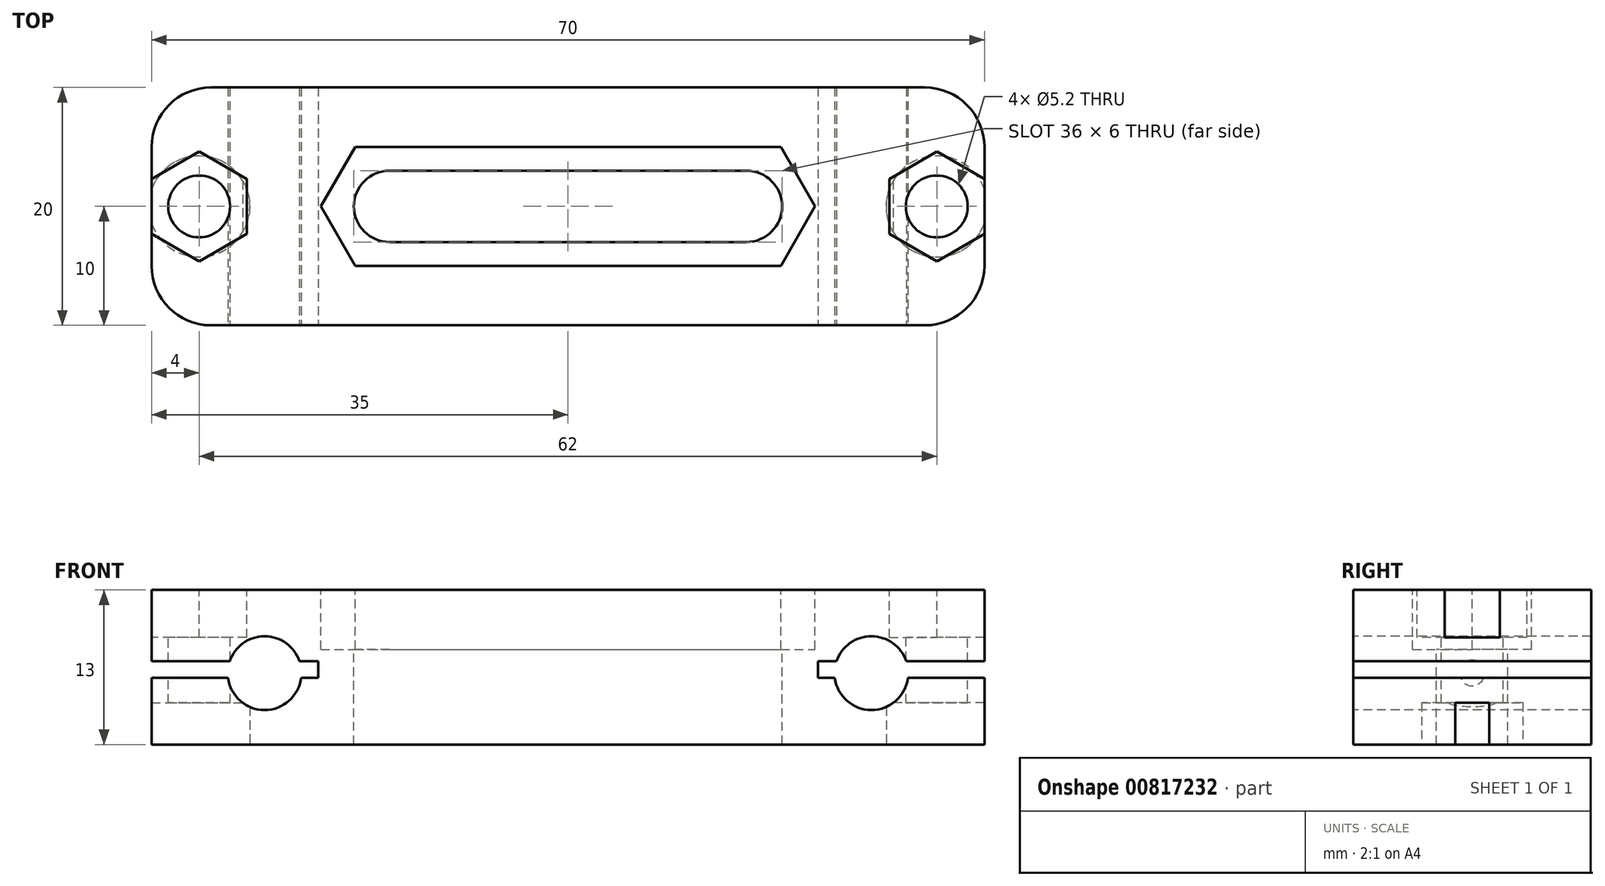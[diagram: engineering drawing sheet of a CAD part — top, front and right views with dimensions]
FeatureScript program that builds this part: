
annotation { "Feature Type Name" : "Feature", "Feature Type Description" : "" }
export const myFeature = defineFeature(function(context is Context, id is Id, definition is map)
    precondition{}
    {
        {
            var Q0;
            Q0=qCreatedBy(makeId("Top.planeOp"),FACE);
            var sketch = newSketch(context, id + "F0", { "sketchPlane" : qUnion([Q0])});
            skLineSegment(sketch, "E0.bottom", {"start": v(35, -10) * mm, "end": v(-35, -10) * mm});
            skLineSegment(sketch, "E0.top", {"start": v(35, 10) * mm, "end": v(-35, 10) * mm});
            skLineSegment(sketch, "E0.left", {"start": v(35, -10) * mm, "end": v(35, 10) * mm});
            skLineSegment(sketch, "E0.right", {"start": v(-35, -10) * mm, "end": v(-35, 10) * mm});
            skPoint(sketch, "E0.middle", {"position": v(0, 0) * mm});
            skSolve(sketch);
        }
        {
            var Q0;
            Q0=qSketchRegion(id+"F0",true);
            extrude(context, id + "F1", {"entities" : qUnion([Q0]), "endBound" : BoundingType.SYMMETRIC, "depth" : 13 * mm, "offsetDistance" : 25 * mm});
        }
        {
            var Q0;
            Q0=makeQuery(id+"F1.opExtrude","CAP_FACE",FACE,{"disambiguationData":[OSD([sQuery(id+"F0.wireOp",EDGE,"E0.bottom"),sQuery(id+"F0.wireOp",EDGE,"E0.top"),sQuery(id+"F0.wireOp",EDGE,"E0.left"),sQuery(id+"F0.wireOp",EDGE,"E0.right")])],"isStart":false});
            var sketch = newSketch(context, id + "F2", { "sketchPlane" : qUnion([Q0])});
            skLineSegment(sketch, "E1.bottom", {"start": v(15, -3) * mm, "end": v(-15, -3) * mm});
            skLineSegment(sketch, "E1.top", {"start": v(15, 3) * mm, "end": v(-15, 3) * mm});
            skPoint(sketch, "E1.middle", {"position": v(0, 0) * mm});
            skArc(sketch, "E2", {"start": v(-15, 3) * mm, "mid": v(-18, 0) * mm, "end": v(-15, -3) * mm});
            skArc(sketch, "E3", {"start": v(15, 3) * mm, "mid": v(18, 0) * mm, "end": v(15, -3) * mm});
            skSolve(sketch);
        }
        {
            var Q0;
            Q0=makeQuery(id+"F2.imprint","IMPRINT",FACE,{"disambiguationData":[TD([[makeQuery(id+"F2.imprint","IMPRINT",EDGE,{"derivedFrom":sQuery(id+"F2.wireOp",EDGE,"E1.bottom")}),1.0]])]});
            var sketch = newSketch(context, id + "F3", { "sketchPlane" : qUnion([Q0])});
            skCircle(sketch, "E4.cCircle", {"center": v(-31, 0) * mm, "radius": 4 * mm, "construction": true});
            skLineSegment(sketch, "E4.0", {"start": v(-27, -2.3) * mm, "end": v(-31, -4.62) * mm});
            skLineSegment(sketch, "E4.1", {"start": v(-31, -4.62) * mm, "end": v(-35, -2.3) * mm});
            skLineSegment(sketch, "E4.2", {"start": v(-35, -2.3) * mm, "end": v(-35, 2.3) * mm});
            skLineSegment(sketch, "E4.3", {"start": v(-35, 2.3) * mm, "end": v(-31, 4.62) * mm});
            skLineSegment(sketch, "E4.4", {"start": v(-31, 4.62) * mm, "end": v(-27, 2.3) * mm});
            skLineSegment(sketch, "E4.5", {"start": v(-27, 2.3) * mm, "end": v(-27, -2.3) * mm});
            skPoint(sketch, "E4.0.midPoint", {"position": v(-29, -3.46) * mm});
            skCircle(sketch, "E5.cCircle", {"center": v(31, 0) * mm, "radius": 4 * mm, "construction": true});
            skLineSegment(sketch, "E5.0", {"start": v(35, 2.3) * mm, "end": v(35, -2.3) * mm});
            skLineSegment(sketch, "E5.1", {"start": v(35, -2.3) * mm, "end": v(31, -4.62) * mm});
            skLineSegment(sketch, "E5.2", {"start": v(31, -4.62) * mm, "end": v(27, -2.3) * mm});
            skLineSegment(sketch, "E5.3", {"start": v(27, -2.3) * mm, "end": v(27, 2.3) * mm});
            skLineSegment(sketch, "E5.4", {"start": v(27, 2.3) * mm, "end": v(31, 4.62) * mm});
            skLineSegment(sketch, "E5.5", {"start": v(31, 4.62) * mm, "end": v(35, 2.3) * mm});
            skPoint(sketch, "E5.0.midPoint", {"position": v(35, 0) * mm});
            skSolve(sketch);
        }
        {
            var Q0;
            Q0=qSketchRegion(id+"F3",true);
            extrude(context, id + "F4", {"entities" : qUnion([Q0]), "operationType" : NewBodyOperationType.REMOVE, "oppositeDirection" : true, "depth" : 4 * mm, "offsetDistance" : 25 * mm});
        }
        {
            var Q0;
            Q0=makeQuery(id+"F2.imprint","IMPRINT",FACE,{"disambiguationData":[TD([[makeQuery(id+"F2.imprint","IMPRINT",EDGE,{"derivedFrom":sQuery(id+"F2.wireOp",EDGE,"E1.bottom")}),1.0]])]});
            var sketch = newSketch(context, id + "F5", { "sketchPlane" : qUnion([Q0])});
            skCircle(sketch, "E6", {"center": v(-31, 0) * mm, "radius": 2.6 * mm});
            skCircle(sketch, "E7", {"center": v(31, 0) * mm, "radius": 2.6 * mm});
            skSolve(sketch);
        }
        {
            var Q0;
            Q0=qSketchRegion(id+"F5",true);
            extrude(context, id + "F6", {"entities" : qUnion([Q0]), "operationType" : NewBodyOperationType.REMOVE, "endBound" : BoundingType.THROUGH_ALL, "oppositeDirection" : true, "depth" : 25 * mm, "offsetDistance" : 25 * mm});
        }
        {
            var Q0;
            Q0=qSketchRegion(id+"F2",true);
            extrude(context, id + "F7", {"entities" : qUnion([Q0]), "operationType" : NewBodyOperationType.REMOVE, "endBound" : BoundingType.THROUGH_ALL, "oppositeDirection" : true, "depth" : 25 * mm, "offsetDistance" : 25 * mm});
        }
        {
            var Q0;
            Q0=makeQuery(id+"F1.opExtrude","SWEPT_FACE",FACE,{"disambiguationData":[OSD([sQuery(id+"F0.wireOp",EDGE,"E0.bottom")])]});
            var sketch = newSketch(context, id + "F8", { "sketchPlane" : qUnion([Q0])});
            skLineSegment(sketch, "E8.bottom", {"start": v(-35, -0.9) * mm, "end": v(-21, -0.9) * mm});
            skLineSegment(sketch, "E8.top", {"start": v(-35, 0.5) * mm, "end": v(-21, 0.5) * mm});
            skLineSegment(sketch, "E8.left", {"start": v(-35, -0.9) * mm, "end": v(-35, 0.5) * mm});
            skLineSegment(sketch, "E8.right", {"start": v(-21, -0.9) * mm, "end": v(-21, 0.5) * mm});
            skLineSegment(sketch, "E9.bottom", {"start": v(35, -0.9) * mm, "end": v(21, -0.9) * mm});
            skLineSegment(sketch, "E9.top", {"start": v(35, 0.5) * mm, "end": v(21, 0.5) * mm});
            skLineSegment(sketch, "E9.left", {"start": v(35, -0.9) * mm, "end": v(35, 0.5) * mm});
            skLineSegment(sketch, "E9.right", {"start": v(21, -0.9) * mm, "end": v(21, 0.5) * mm});
            skSolve(sketch);
        }
        {
            var Q0;
            Q0=qSketchRegion(id+"F8",true);
            extrude(context, id + "F9", {"entities" : qUnion([Q0]), "operationType" : NewBodyOperationType.REMOVE, "endBound" : BoundingType.THROUGH_ALL, "oppositeDirection" : true, "depth" : 25 * mm, "offsetDistance" : 25 * mm});
        }
        {
            var Q0;
            Q0=makeQuery(id+"F1.opExtrude","SWEPT_FACE",FACE,{"disambiguationData":[OSD([sQuery(id+"F0.wireOp",EDGE,"E0.bottom")])]});
            var sketch = newSketch(context, id + "F10", { "sketchPlane" : qUnion([Q0])});
            skCircle(sketch, "E10", {"center": v(-25.5, -0.5) * mm, "radius": 3.1 * mm});
            skCircle(sketch, "E11", {"center": v(25.5, -0.5) * mm, "radius": 3.1 * mm});
            skSolve(sketch);
        }
        {
            var Q0;
            Q0=makeQuery(id+"FGKyORt9fG3GxLQ_1.opExtrude","CAP_EDGE",EDGE,{"disambiguationData":[OSD([sQuery(id+"FUYUVBWRlq5jCbc_1.wireOp",EDGE,"ZpnfMVQ8-PDP1-Nz7W-Utch-BhDVuRkNCdpB.left")])],"isStart":false});
            var Q1;
            {var subQ0=sQuery(id+"F0.wireOp",EDGE,"E0.left");var subQ1=sQuery(id+"F0.wireOp",EDGE,"E0.top");Q1=makeQuery(id+"F9.boolean.opBoolean","SPLIT",EDGE,{"disambiguationData":[TD([makeQuery(id+"F9.opExtrude","SWEPT_FACE",FACE,{"disambiguationData":[OSD([sQuery(id+"F8.wireOp",EDGE,"E9.top")])]})])],"derivedFrom":makeQuery(id+"F1.opExtrude","SWEPT_EDGE",EDGE,{"disambiguationData":[OSD([subQ1,subQ0])]})});}
            var Q2;
            {var subQ0=sQuery(id+"F0.wireOp",EDGE,"E0.left");var subQ1=sQuery(id+"F0.wireOp",EDGE,"E0.top");Q2=makeQuery(id+"F9.boolean.opBoolean","SPLIT",EDGE,{"disambiguationData":[TD([makeQuery(id+"F9.opExtrude","SWEPT_FACE",FACE,{"disambiguationData":[OSD([sQuery(id+"F8.wireOp",EDGE,"E9.bottom")])]})])],"derivedFrom":makeQuery(id+"F1.opExtrude","SWEPT_EDGE",EDGE,{"disambiguationData":[OSD([subQ1,subQ0])]})});}
            var Q3;
            {var subQ0=sQuery(id+"F0.wireOp",EDGE,"E0.bottom");var subQ1=sQuery(id+"F0.wireOp",EDGE,"E0.left");Q3=makeQuery(id+"F9.boolean.opBoolean","SPLIT",EDGE,{"disambiguationData":[TD([makeQuery(id+"F9.opExtrude","SWEPT_FACE",FACE,{"disambiguationData":[OSD([sQuery(id+"F8.wireOp",EDGE,"E9.top")])]})])],"derivedFrom":makeQuery(id+"F1.opExtrude","SWEPT_EDGE",EDGE,{"disambiguationData":[OSD([subQ0,subQ1])]})});}
            var Q4;
            {var subQ0=sQuery(id+"F0.wireOp",EDGE,"E0.bottom");var subQ1=sQuery(id+"F0.wireOp",EDGE,"E0.left");Q4=makeQuery(id+"F9.boolean.opBoolean","SPLIT",EDGE,{"disambiguationData":[TD([makeQuery(id+"F9.opExtrude","SWEPT_FACE",FACE,{"disambiguationData":[OSD([sQuery(id+"F8.wireOp",EDGE,"E9.bottom")])]})])],"derivedFrom":makeQuery(id+"F1.opExtrude","SWEPT_EDGE",EDGE,{"disambiguationData":[OSD([subQ0,subQ1])]})});}
            var Q5;
            {var subQ0=sQuery(id+"F0.wireOp",EDGE,"E0.bottom");var subQ1=sQuery(id+"F0.wireOp",EDGE,"E0.right");Q5=makeQuery(id+"F9.boolean.opBoolean","SPLIT",EDGE,{"disambiguationData":[TD([makeQuery(id+"F9.opExtrude","SWEPT_FACE",FACE,{"disambiguationData":[OSD([sQuery(id+"F8.wireOp",EDGE,"E8.bottom")])]})])],"derivedFrom":makeQuery(id+"F1.opExtrude","SWEPT_EDGE",EDGE,{"disambiguationData":[OSD([subQ0,subQ1])]})});}
            var Q6;
            {var subQ0=sQuery(id+"F0.wireOp",EDGE,"E0.bottom");var subQ1=sQuery(id+"F0.wireOp",EDGE,"E0.right");Q6=makeQuery(id+"F9.boolean.opBoolean","SPLIT",EDGE,{"disambiguationData":[TD([makeQuery(id+"F9.opExtrude","SWEPT_FACE",FACE,{"disambiguationData":[OSD([sQuery(id+"F8.wireOp",EDGE,"E8.top")])]})])],"derivedFrom":makeQuery(id+"F1.opExtrude","SWEPT_EDGE",EDGE,{"disambiguationData":[OSD([subQ0,subQ1])]})});}
            var Q7;
            {var subQ0=sQuery(id+"F0.wireOp",EDGE,"E0.right");var subQ1=sQuery(id+"F0.wireOp",EDGE,"E0.top");Q7=makeQuery(id+"F9.boolean.opBoolean","SPLIT",EDGE,{"disambiguationData":[TD([makeQuery(id+"F9.opExtrude","SWEPT_FACE",FACE,{"disambiguationData":[OSD([sQuery(id+"F8.wireOp",EDGE,"E8.top")])]})])],"derivedFrom":makeQuery(id+"F1.opExtrude","SWEPT_EDGE",EDGE,{"disambiguationData":[OSD([subQ1,subQ0])]})});}
            var Q8;
            {var subQ0=sQuery(id+"F0.wireOp",EDGE,"E0.right");var subQ1=sQuery(id+"F0.wireOp",EDGE,"E0.top");Q8=makeQuery(id+"F9.boolean.opBoolean","SPLIT",EDGE,{"disambiguationData":[TD([makeQuery(id+"F9.opExtrude","SWEPT_FACE",FACE,{"disambiguationData":[OSD([sQuery(id+"F8.wireOp",EDGE,"E8.bottom")])]})])],"derivedFrom":makeQuery(id+"F1.opExtrude","SWEPT_EDGE",EDGE,{"disambiguationData":[OSD([subQ1,subQ0])]})});}
            var Q9;
            Q9=makeQuery(id+"FGKyORt9fG3GxLQ_1.opExtrude","CAP_EDGE",EDGE,{"disambiguationData":[OSD([sQuery(id+"FUYUVBWRlq5jCbc_1.wireOp",EDGE,"ZpnfMVQ8-PDP1-Nz7W-Utch-BhDVuRkNCdpB.right")])],"isStart":false});
            fillet(context, id + "F11", {"entities" : qUnion([Q0, Q1, Q2, Q3, Q4, Q5, Q6, Q7, Q8, Q9]), "radius" : 5 * mm, "tangentPropagation" : true, "allowEdgeOverflow" : false});
        }
        {
            var Q0;
            Q0=qSketchRegion(id+"F10",true);
            extrude(context, id + "F12", {"entities" : qUnion([Q0]), "operationType" : NewBodyOperationType.REMOVE, "endBound" : BoundingType.THROUGH_ALL, "oppositeDirection" : true, "depth" : 25 * mm, "offsetDistance" : 25 * mm});
        }
        {
            var Q0;
            Q0=makeQuery(id+"F1.opExtrude","CAP_FACE",FACE,{"disambiguationData":[OSD([sQuery(id+"F0.wireOp",EDGE,"E0.bottom"),sQuery(id+"F0.wireOp",EDGE,"E0.top"),sQuery(id+"F0.wireOp",EDGE,"E0.left"),sQuery(id+"F0.wireOp",EDGE,"E0.right")])],"isStart":true});
            var sketch = newSketch(context, id + "F13", { "sketchPlane" : qUnion([Q0])});
            skCircle(sketch, "E12", {"center": v(31, 0) * mm, "radius": 4.25 * mm});
            skCircle(sketch, "E13", {"center": v(-31, 0) * mm, "radius": 4.25 * mm});
            skSolve(sketch);
        }
        {
            var Q0;
            Q0=qSketchRegion(id+"F13",true);
            extrude(context, id + "F14", {"entities" : qUnion([Q0]), "operationType" : NewBodyOperationType.REMOVE, "oppositeDirection" : true, "depth" : 3.5 * mm, "offsetDistance" : 25 * mm});
        }
        {
            var Q0;
            Q0=makeQuery(id+"F1.opExtrude","CAP_FACE",FACE,{"disambiguationData":[OSD([sQuery(id+"F0.wireOp",EDGE,"E0.bottom"),sQuery(id+"F0.wireOp",EDGE,"E0.top"),sQuery(id+"F0.wireOp",EDGE,"E0.left"),sQuery(id+"F0.wireOp",EDGE,"E0.right")])],"isStart":false});
            var sketch = newSketch(context, id + "F15", { "sketchPlane" : qUnion([Q0])});
            skCircle(sketch, "E14.cCircle", {"center": v(-15, 0) * mm, "radius": 5 * mm, "construction": true});
            skLineSegment(sketch, "E14.0", {"start": v(-12.11, -5) * mm, "end": v(-17.89, -5) * mm});
            skLineSegment(sketch, "E14.1", {"start": v(-17.89, -5) * mm, "end": v(-20.77, 0) * mm});
            skLineSegment(sketch, "E14.2", {"start": v(-20.77, 0) * mm, "end": v(-17.89, 5) * mm});
            skLineSegment(sketch, "E14.3", {"start": v(-17.89, 5) * mm, "end": v(-12.11, 5) * mm});
            skLineSegment(sketch, "E14.4", {"start": v(-12.11, 5) * mm, "end": v(-9.23, 0) * mm});
            skLineSegment(sketch, "E14.5", {"start": v(-9.23, 0) * mm, "end": v(-12.11, -5) * mm});
            skPoint(sketch, "E14.0.midPoint", {"position": v(-15, -5) * mm});
            skCircle(sketch, "E15.cCircle", {"center": v(15, 0) * mm, "radius": 5 * mm, "construction": true});
            skLineSegment(sketch, "E15.0", {"start": v(17.89, -5) * mm, "end": v(12.11, -5) * mm});
            skLineSegment(sketch, "E15.1", {"start": v(12.11, -5) * mm, "end": v(9.23, 0) * mm});
            skLineSegment(sketch, "E15.2", {"start": v(9.23, 0) * mm, "end": v(12.11, 5) * mm});
            skLineSegment(sketch, "E15.3", {"start": v(12.11, 5) * mm, "end": v(17.89, 5) * mm});
            skLineSegment(sketch, "E15.4", {"start": v(17.89, 5) * mm, "end": v(20.77, 0) * mm});
            skLineSegment(sketch, "E15.5", {"start": v(20.77, 0) * mm, "end": v(17.89, -5) * mm});
            skPoint(sketch, "E15.0.midPoint", {"position": v(15, -5) * mm});
            skLineSegment(sketch, "E16", {"start": v(-12.11, 5) * mm, "end": v(12.11, 5) * mm});
            skLineSegment(sketch, "E17", {"start": v(12.11, -5) * mm, "end": v(-12.11, -5) * mm});
            skSolve(sketch);
        }
        {
            var Q0;
            Q0 = qSketchRegion(id + "F15", true);
            extrude(context, id + "F16", {"entities" : qUnion([Q0]), "operationType" : NewBodyOperationType.REMOVE, "oppositeDirection" : true, "depth" : 5 * mm, "offsetDistance" : 25 * mm});
        }
    });
